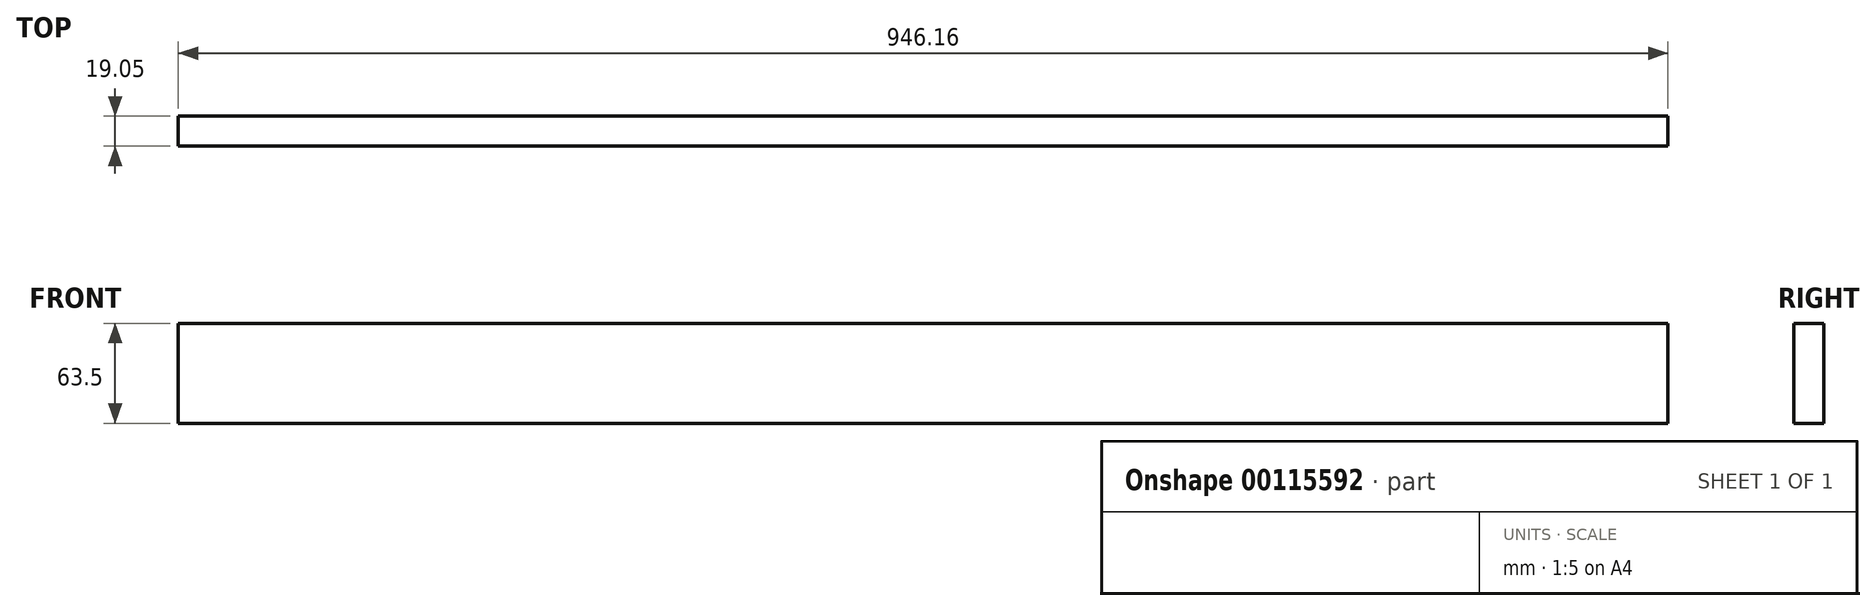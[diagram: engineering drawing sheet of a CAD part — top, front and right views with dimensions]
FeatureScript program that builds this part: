
annotation { "Feature Type Name" : "Feature", "Feature Type Description" : "" }
export const myFeature = defineFeature(function(context is Context, id is Id, definition is map)
    precondition{}
    {
        {
            var Q0;
            Q0=qCreatedBy(makeId("Front.planeOp"),FACE);
            var sketch = newSketch(context, id + "F0", { "sketchPlane" : qUnion([Q0])});
            skLineSegment(sketch, "E0.bottom", {"start": v(-473.08, 31.75) * mm, "end": v(473.08, 31.75) * mm});
            skLineSegment(sketch, "E0.top", {"start": v(-473.08, -31.75) * mm, "end": v(473.08, -31.75) * mm});
            skLineSegment(sketch, "E0.left", {"start": v(-473.08, 31.75) * mm, "end": v(-473.08, -31.75) * mm});
            skLineSegment(sketch, "E0.right", {"start": v(473.08, 31.75) * mm, "end": v(473.08, -31.75) * mm});
            skPoint(sketch, "E0.middle", {"position": v(0, 0) * mm});
            skSolve(sketch);
        }
        {
            var Q0;
            Q0=makeQuery(id+"F0.imprint","IMPRINT",FACE,{"disambiguationData":[TD([[makeQuery(id+"F0.imprint","IMPRINT",EDGE,{"derivedFrom":sQuery(id+"F0.wireOp",EDGE,"E0.bottom")}),-1.0]])]});
            extrude(context, id + "F1", {"entities" : qUnion([Q0]), "depth" : 19.05 * mm});
        }
    });
